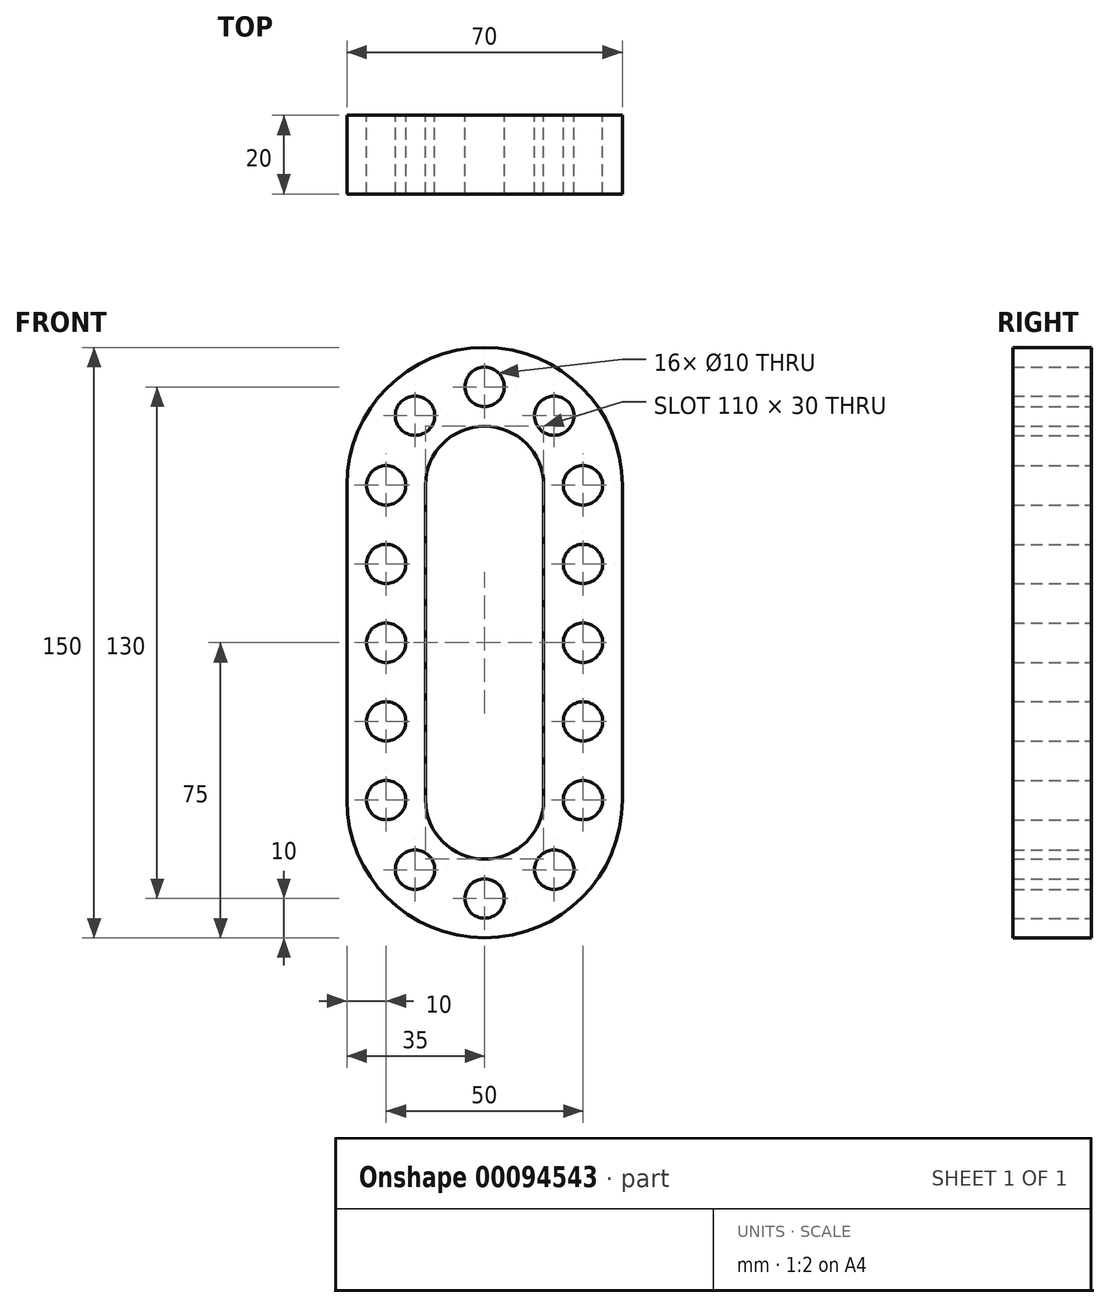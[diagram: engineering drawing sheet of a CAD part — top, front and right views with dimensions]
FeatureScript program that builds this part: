
annotation { "Feature Type Name" : "Feature", "Feature Type Description" : "" }
export const myFeature = defineFeature(function(context is Context, id is Id, definition is map)
    precondition{}
    {
        {
            var Q0;
            Q0=qCreatedBy(makeId("Front.planeOp"),FACE);
            var sketch = newSketch(context, id + "F0", { "sketchPlane" : qUnion([Q0])});
            skPoint(sketch, "E0", {"position": v(-25, 40) * mm});
            skArc(sketch, "E1", {"start": v(0, 65) * mm, "mid": v(-17.68, 57.68) * mm, "end": v(-25, 40) * mm, "construction": true});
            skLineSegment(sketch, "E2", {"start": v(-25, 40) * mm, "end": v(-25, 0) * mm, "construction": true});
            skArc(sketch, "E3.0.startCap", {"start": v(0, 75) * mm, "mid": v(10, 65) * mm, "end": v(0, 55) * mm, "construction": true});
            skArc(sketch, "E3.0.endCap", {"start": v(-15, 40) * mm, "mid": v(-25, 30) * mm, "end": v(-35, 40) * mm, "construction": true});
            skArc(sketch, "E3.0.left", {"start": v(0, 55) * mm, "mid": v(-10.6, 50.6) * mm, "end": v(-15, 40) * mm});
            skArc(sketch, "E3.0.right", {"start": v(0, 75) * mm, "mid": v(-24.75, 64.75) * mm, "end": v(-35, 40) * mm});
            skArc(sketch, "E3.1.startCap", {"start": v(-35, 40) * mm, "mid": v(-25, 50) * mm, "end": v(-15, 40) * mm, "construction": true});
            skArc(sketch, "E3.1.endCap", {"start": v(-15, 0) * mm, "mid": v(-25, -10) * mm, "end": v(-35, 0) * mm, "construction": true});
            skLineSegment(sketch, "E3.1.left", {"start": v(-15, 40) * mm, "end": v(-15, 0) * mm});
            skLineSegment(sketch, "E3.1.right", {"start": v(-35, 40) * mm, "end": v(-35, 0) * mm});
            skCircle(sketch, "E4", {"center": v(-25, 40) * mm, "radius": 5 * mm});
            skCircle(sketch, "E5.0.1.0", {"center": v(-25, 20) * mm, "radius": 5 * mm});
            skCircle(sketch, "E5.0.2.0", {"center": v(-25, 0) * mm, "radius": 5 * mm});
            skLineSegment(sketch, "E5.direction1", {"start": v(-25, 40) * mm, "end": v(0, 40) * mm, "construction": true});
            skLineSegment(sketch, "E5.direction2", {"start": v(-25, 40) * mm, "end": v(-25, 20) * mm, "construction": true});
            skCircle(sketch, "E6.1.0", {"center": v(-17.68, 57.68) * mm, "radius": 5 * mm});
            skCircle(sketch, "E6.2.0", {"center": v(0, 65) * mm, "radius": 5 * mm});
            skLineSegment(sketch, "E6.anchor1", {"start": v(0, 40) * mm, "end": v(-25, 40) * mm, "construction": true});
            skLineSegment(sketch, "E6.anchor2", {"start": v(0, 40) * mm, "end": v(0, 65) * mm, "construction": true});
            skLineSegment(sketch, "E7", {"start": v(-35, 0) * mm, "end": v(-30, 0) * mm});
            skLineSegment(sketch, "E8", {"start": v(-15, 0) * mm, "end": v(-20, 0) * mm});
            skLineSegment(sketch, "E9", {"start": v(0, 75) * mm, "end": v(0, 70) * mm});
            skLineSegment(sketch, "E10", {"start": v(0, 55) * mm, "end": v(0, 60) * mm});
            skSolve(sketch);
        }
        {
            var Q0;
            Q0=makeQuery(id+"F0.imprint","IMPRINT",FACE,{"disambiguationData":[TD([[makeQuery(id+"F0.imprint","IMPRINT",EDGE,{"derivedFrom":sQuery(id+"F0.wireOp",EDGE,"E3.0.left")}),-1.0]])]});
            extrude(context, id + "F1", {"entities" : qUnion([Q0]), "depth" : 20 * mm});
        }
        {
            var Q0;
            Q0=makeQuery(id+"F1.opExtrude","SWEPT_BODY",BODY,{"disambiguationData":[OSD([sQuery(id+"F0.wireOp",EDGE,"E3.0.left"),sQuery(id+"F0.wireOp",EDGE,"E3.0.right"),sQuery(id+"F0.wireOp",EDGE,"E3.1.left"),sQuery(id+"F0.wireOp",EDGE,"E3.1.right"),sQuery(id+"F0.wireOp",EDGE,"E4"),sQuery(id+"F0.wireOp",EDGE,"E5.0.1.0"),sQuery(id+"F0.wireOp",EDGE,"E5.0.2.0"),sQuery(id+"F0.wireOp",EDGE,"E6.1.0"),sQuery(id+"F0.wireOp",EDGE,"E6.2.0"),sQuery(id+"F0.wireOp",EDGE,"E7"),sQuery(id+"F0.wireOp",EDGE,"E8"),sQuery(id+"F0.wireOp",EDGE,"E9"),sQuery(id+"F0.wireOp",EDGE,"E10")])]});
            var Q1;
            Q1=qCreatedBy(makeId("Right.planeOp"),FACE);
            mirror(context, id + "F2", {"operationType" : NewBodyOperationType.ADD, "entities" : qUnion([Q0]), "mirrorPlane" : qUnion([Q1])});
        }
        {
            var Q0;
            Q0=makeQuery(id+"F1.opExtrude","SWEPT_BODY",BODY,{"disambiguationData":[OSD([sQuery(id+"F0.wireOp",EDGE,"E3.0.left"),sQuery(id+"F0.wireOp",EDGE,"E3.0.right"),sQuery(id+"F0.wireOp",EDGE,"E3.1.left"),sQuery(id+"F0.wireOp",EDGE,"E3.1.right"),sQuery(id+"F0.wireOp",EDGE,"E4"),sQuery(id+"F0.wireOp",EDGE,"E5.0.1.0"),sQuery(id+"F0.wireOp",EDGE,"E5.0.2.0"),sQuery(id+"F0.wireOp",EDGE,"E6.1.0"),sQuery(id+"F0.wireOp",EDGE,"E6.2.0"),sQuery(id+"F0.wireOp",EDGE,"E7"),sQuery(id+"F0.wireOp",EDGE,"E8"),sQuery(id+"F0.wireOp",EDGE,"E9"),sQuery(id+"F0.wireOp",EDGE,"E10")])]});
            var Q1;
            Q1=qCreatedBy(makeId("Top.planeOp"),FACE);
            mirror(context, id + "F3", {"operationType" : NewBodyOperationType.ADD, "entities" : qUnion([Q0]), "mirrorPlane" : qUnion([Q1])});
        }
    });
